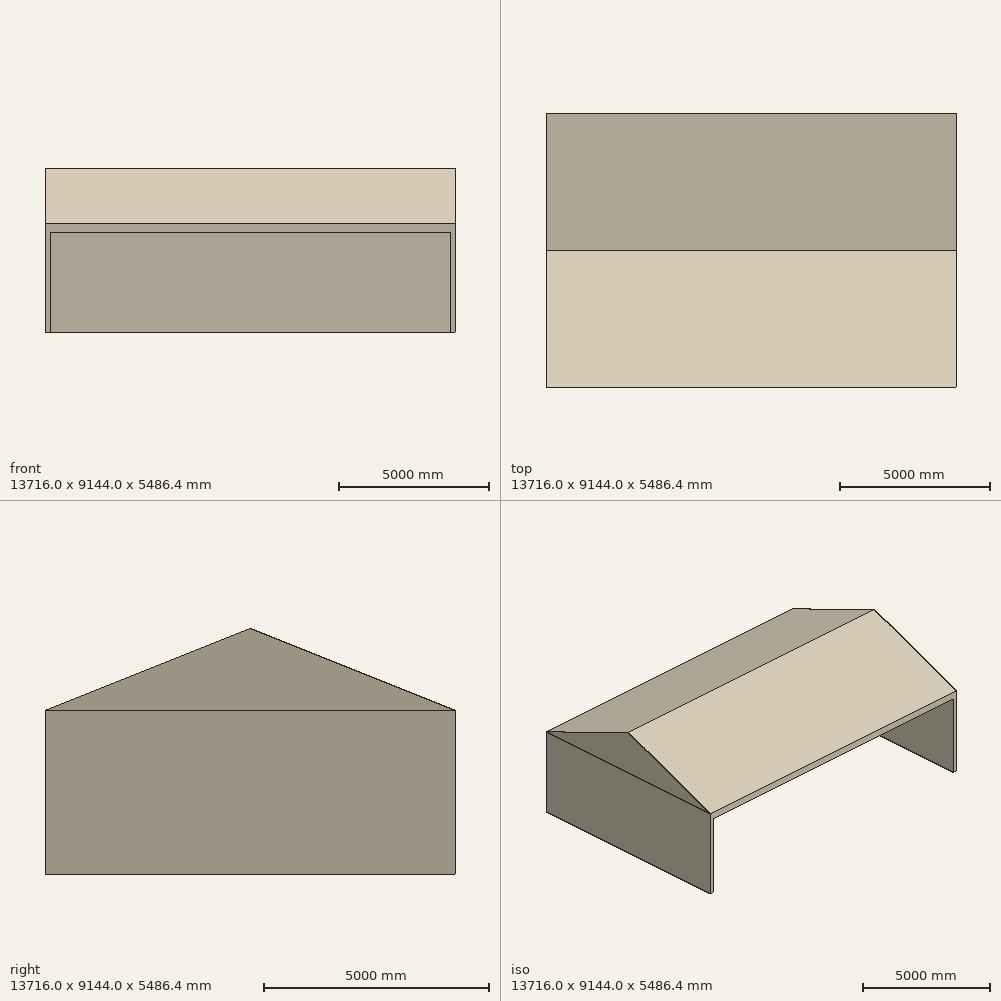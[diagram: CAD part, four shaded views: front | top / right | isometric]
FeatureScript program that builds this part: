
annotation { "Feature Type Name" : "Feature", "Feature Type Description" : "" }
export const myFeature = defineFeature(function(context is Context, id is Id, definition is map)
    precondition{}
    {
        {
            var Q0;
            Q0=qCreatedBy(makeId("Front.planeOp"),FACE);
            var sketch = newSketch(context, id + "F0", { "sketchPlane" : qUnion([Q0])});
            skLineSegment(sketch, "E0", {"start": v(-4384.45, -1815.36) * mm, "end": v(9331.55, -1815.36) * mm});
            skLineSegment(sketch, "E1", {"start": v(9331.55, -1815.36) * mm, "end": v(9331.55, 1842.24) * mm});
            skLineSegment(sketch, "E2", {"start": v(9331.55, 1842.24) * mm, "end": v(-4384.45, 1842.24) * mm});
            skLineSegment(sketch, "E3", {"start": v(-4384.45, 1842.24) * mm, "end": v(-4384.45, -1815.36) * mm});
            skSolve(sketch);
        }
        {
            var Q0;
            Q0 = qSketchRegion(id + "F0", true);
            extrude(context, id + "F1", {"entities" : qUnion([Q0]), "depth" : 9144 * mm});
        }
        {
            var Q0;
            Q0=makeQuery(id+"F1.opExtrude","SWEPT_FACE",FACE,{"disambiguationData":[OSD([sQuery(id+"F0.wireOp",EDGE,"E1")])]});
            var sketch = newSketch(context, id + "F2", { "sketchPlane" : qUnion([Q0])});
            skLineSegment(sketch, "E4", {"start": v(-4572, 1842.24) * mm, "end": v(-4572, 3671.04) * mm});
            skPoint(sketch, "E4.endSnap0", {"position": v(-4572, 1842.24) * mm});
            skLineSegment(sketch, "E5", {"start": v(-4572, 3671.04) * mm, "end": v(-9144, 1842.24) * mm});
            skLineSegment(sketch, "E6", {"start": v(-4572, 3671.04) * mm, "end": v(0, 1842.24) * mm});
            skSolve(sketch);
        }
        {
            var Q0;
            {var subQ0=sQuery(id+"F2.wireOp",EDGE,"E4");Q0=makeQuery(id+"F2.imprint","IMPRINT",FACE,{"disambiguationData":[TD([[makeQuery(id+"F2.imprint","IMPRINT",EDGE,{"derivedFrom":subQ0}),1.0]])]});}
            var Q1;
            {var subQ0=sQuery(id+"F2.wireOp",EDGE,"E4");Q1=makeQuery(id+"F2.imprint","IMPRINT",FACE,{"disambiguationData":[TD([[makeQuery(id+"F2.imprint","IMPRINT",EDGE,{"derivedFrom":subQ0}),-1.0]])]});}
            extrude(context, id + "F3", {"entities" : qUnion([Q0, Q1]), "oppositeDirection" : true, "depth" : 13716 * mm});
        }
        {
            var Q0;
            Q0=makeQuery(id+"F1.opExtrude","CAP_FACE",FACE,{"disambiguationData":[OSD([sQuery(id+"F0.wireOp",EDGE,"E0"),sQuery(id+"F0.wireOp",EDGE,"E1"),sQuery(id+"F0.wireOp",EDGE,"E2"),sQuery(id+"F0.wireOp",EDGE,"E3")])],"isStart":false});
            var sketch = newSketch(context, id + "F4", { "sketchPlane" : qUnion([Q0])});
            skLineSegment(sketch, "E7", {"start": v(-4232.05, -1815.36) * mm, "end": v(-4232.05, 1537.44) * mm});
            skLineSegment(sketch, "E8", {"start": v(-4232.05, 1537.44) * mm, "end": v(9179.15, 1537.44) * mm});
            skLineSegment(sketch, "E9", {"start": v(9179.15, 1537.44) * mm, "end": v(9179.15, -1815.36) * mm});
            skSolve(sketch);
        }
        {
            var Q0;
            {var subQ0=sQuery(id+"F4.wireOp",EDGE,"E7");Q0=makeQuery(id+"F4.imprint","IMPRINT",FACE,{"disambiguationData":[TD([[makeQuery(id+"F4.imprint","IMPRINT",EDGE,{"derivedFrom":subQ0}),-1.0]])]});}
            extrude(context, id + "F5", {"entities" : qUnion([Q0]), "operationType" : NewBodyOperationType.REMOVE, "oppositeDirection" : true, "depth" : 8839.2 * mm});
        }
    });
